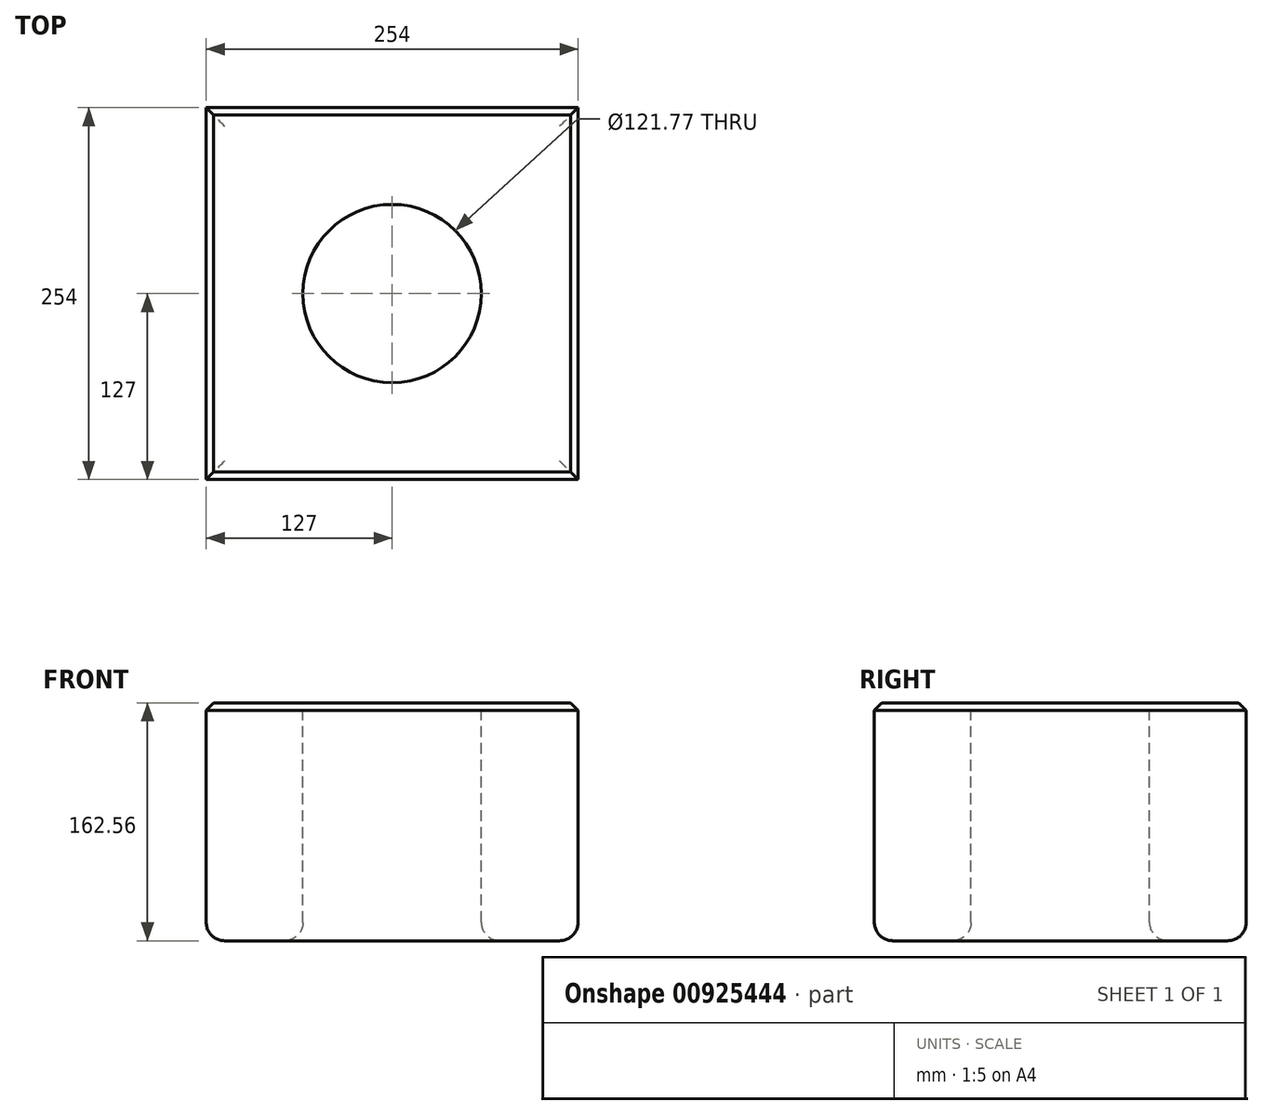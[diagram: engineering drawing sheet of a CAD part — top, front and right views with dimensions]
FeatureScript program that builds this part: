
annotation { "Feature Type Name" : "Feature", "Feature Type Description" : "" }
export const myFeature = defineFeature(function(context is Context, id is Id, definition is map)
    precondition{}
    {
        {
            var Q0;
            Q0=qCreatedBy(makeId("Top.planeOp"),FACE);
            var sketch = newSketch(context, id + "F0", { "sketchPlane" : qUnion([Q0])});
            skLineSegment(sketch, "E0.bottom", {"start": v(127, 127) * mm, "end": v(-127, 127) * mm});
            skLineSegment(sketch, "E0.top", {"start": v(127, -127) * mm, "end": v(-127, -127) * mm});
            skLineSegment(sketch, "E0.left", {"start": v(127, 127) * mm, "end": v(127, -127) * mm});
            skLineSegment(sketch, "E0.right", {"start": v(-127, 127) * mm, "end": v(-127, -127) * mm});
            skPoint(sketch, "E0.middle", {"position": v(0, 0) * mm});
            skSolve(sketch);
        }
        {
            var Q0;
            Q0 = qSketchRegion(id + "F0", true);
            extrude(context, id + "F1", {"entities" : qUnion([Q0]), "depth" : 162.56 * mm, "offsetDistance" : 25.4 * mm});
        }
        {
            var Q0;
            Q0=makeQuery(id+"F1.opExtrude","CAP_FACE",FACE,{"disambiguationData":[OSD([sQuery(id+"F0.wireOp",EDGE,"E0.bottom"),sQuery(id+"F0.wireOp",EDGE,"E0.top"),sQuery(id+"F0.wireOp",EDGE,"E0.left"),sQuery(id+"F0.wireOp",EDGE,"E0.right")])],"isStart":false});
            var sketch = newSketch(context, id + "F2", { "sketchPlane" : qUnion([Q0])});
            skCircle(sketch, "E1", {"center": v(0, 0) * mm, "radius": 60.88 * mm});
            skSolve(sketch);
        }
        {
            var Q0;
            Q0 = qSketchRegion(id + "F2", true);
            extrude(context, id + "F3", {"entities" : qUnion([Q0]), "operationType" : NewBodyOperationType.REMOVE, "oppositeDirection" : true, "depth" : 289.56 * mm, "offsetDistance" : 25.4 * mm});
        }
        {
            var Q0;
            Q0=makeQuery(id+"F1.opExtrude","CAP_EDGE",EDGE,{"disambiguationData":[OSD([sQuery(id+"F0.wireOp",EDGE,"E0.left")])],"isStart":false});
            var Q1;
            Q1=makeQuery(id+"F1.opExtrude","CAP_EDGE",EDGE,{"disambiguationData":[OSD([sQuery(id+"F0.wireOp",EDGE,"E0.top")])],"isStart":false});
            var Q2;
            Q2=makeQuery(id+"F1.opExtrude","CAP_EDGE",EDGE,{"disambiguationData":[OSD([sQuery(id+"F0.wireOp",EDGE,"E0.right")])],"isStart":false});
            var Q3;
            Q3=makeQuery(id+"F1.opExtrude","CAP_EDGE",EDGE,{"disambiguationData":[OSD([sQuery(id+"F0.wireOp",EDGE,"E0.bottom")])],"isStart":false});
            var Q4;
            Q4=makeQuery(id+"F3.boolean.opBoolean","COPY",EDGE,{"derivedFrom":makeQuery(id+"F3.opExtrude","CAP_EDGE",EDGE,{"disambiguationData":[OSD([sQuery(id+"F2.wireOp",EDGE,"E1")])],"isStart":true})});
            chamfer(context, id + "F4", {"entities" : qUnion([Q0, Q1, Q2, Q3, Q4]), "width" : 5.08 * mm, "tangentPropagation" : true});
        }
        {
            var Q0;
            Q0=makeQuery(id+"F1.opExtrude","CAP_EDGE",EDGE,{"disambiguationData":[OSD([sQuery(id+"F0.wireOp",EDGE,"E0.right")])],"isStart":true});
            var Q1;
            Q1=makeQuery(id+"F1.opExtrude","CAP_EDGE",EDGE,{"disambiguationData":[OSD([sQuery(id+"F0.wireOp",EDGE,"E0.bottom")])],"isStart":true});
            var Q2;
            Q2=makeQuery(id+"F1.opExtrude","CAP_EDGE",EDGE,{"disambiguationData":[OSD([sQuery(id+"F0.wireOp",EDGE,"E0.left")])],"isStart":true});
            var Q3;
            Q3=makeQuery(id+"F1.opExtrude","CAP_EDGE",EDGE,{"disambiguationData":[OSD([sQuery(id+"F0.wireOp",EDGE,"E0.top")])],"isStart":true});
            fillet(context, id + "F5", {"entities" : qUnion([Q0, Q1, Q2, Q3]), "radius" : 12.7 * mm, "tangentPropagation" : true, "allowEdgeOverflow" : false});
        }
        {
            var Q0;
            Q0=makeQuery(id+"F3.boolean.opBoolean","INTERSECT",EDGE,{"derivedFrom":[makeQuery(id+"F1.opExtrude","CAP_FACE",FACE,{"disambiguationData":[OSD([sQuery(id+"F0.wireOp",EDGE,"E0.bottom"),sQuery(id+"F0.wireOp",EDGE,"E0.top"),sQuery(id+"F0.wireOp",EDGE,"E0.left"),sQuery(id+"F0.wireOp",EDGE,"E0.right")])],"isStart":true}),makeQuery(id+"F3.opExtrude","SWEPT_FACE",FACE,{"disambiguationData":[OSD([sQuery(id+"F2.wireOp",EDGE,"E1")])]})]});
            fillet(context, id + "F6", {"entities" : qUnion([Q0]), "radius" : 12.7 * mm, "tangentPropagation" : true, "allowEdgeOverflow" : false});
        }
    });
